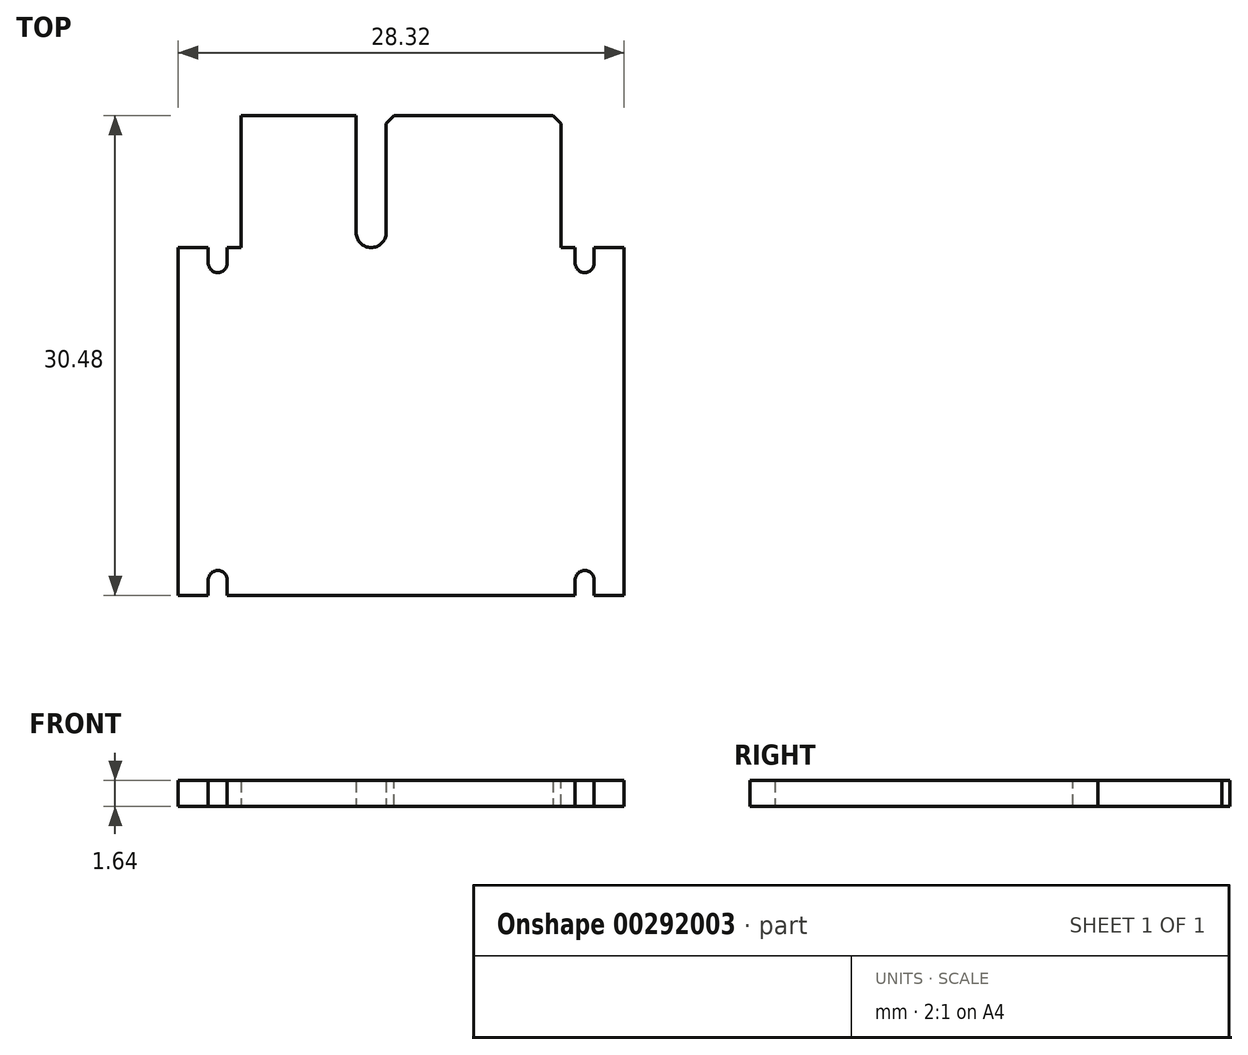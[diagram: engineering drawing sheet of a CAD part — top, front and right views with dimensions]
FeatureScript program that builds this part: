
annotation { "Feature Type Name" : "Feature", "Feature Type Description" : "" }
export const myFeature = defineFeature(function(context is Context, id is Id, definition is map)
    precondition{}
    {
        {
            var Q0;
            Q0=qCreatedBy(makeId("Top.planeOp"),FACE);
            var sketch = newSketch(context, id + "F0", { "sketchPlane" : qUnion([Q0])});
            skLineSegment(sketch, "E0.bottom", {"start": v(14.16, -30.48) * mm, "end": v(-14.16, -30.48) * mm});
            skLineSegment(sketch, "E0.top", {"start": v(14.16, 0) * mm, "end": v(-14.16, 0) * mm});
            skLineSegment(sketch, "E0.left", {"start": v(14.16, -30.48) * mm, "end": v(14.16, 0) * mm});
            skLineSegment(sketch, "E0.right", {"start": v(-14.16, -30.48) * mm, "end": v(-14.16, 0) * mm});
            skPoint(sketch, "E0.middle", {"position": v(0, 0) * mm});
            skSolve(sketch);
        }
        {
            var Q0;
            Q0=qSketchRegion(id+"F0",true);
            extrude(context, id + "F1", {"entities" : qUnion([Q0]), "depth" : 1.64 * mm});
        }
        {
            var Q0;
            Q0=qCreatedBy(makeId("Top.planeOp"),FACE);
            var sketch = newSketch(context, id + "F2", { "sketchPlane" : qUnion([Q0])});
            skLineSegment(sketch, "E1.top", {"start": v(-14.16, 0) * mm, "end": v(-10.16, 0) * mm});
            skLineSegment(sketch, "E1.left", {"start": v(-14.16, -8.38) * mm, "end": v(-14.16, 0) * mm});
            skLineSegment(sketch, "E1.right", {"start": v(-10.16, -8.38) * mm, "end": v(-10.16, 0) * mm});
            skLineSegment(sketch, "E2.bottom", {"start": v(-2.86, -8.38) * mm, "end": v(-0.95, -8.38) * mm});
            skLineSegment(sketch, "E2.top", {"start": v(-2.86, 0) * mm, "end": v(-0.95, 0) * mm});
            skLineSegment(sketch, "E2.left", {"start": v(-2.86, -8.38) * mm, "end": v(-2.86, 0) * mm});
            skLineSegment(sketch, "E2.right", {"start": v(-0.95, -8.38) * mm, "end": v(-0.95, 0) * mm});
            skLineSegment(sketch, "E3.top", {"start": v(14.16, 0) * mm, "end": v(10.16, 0) * mm});
            skLineSegment(sketch, "E3.left", {"start": v(14.16, -8.38) * mm, "end": v(14.16, 0) * mm});
            skLineSegment(sketch, "E3.right", {"start": v(10.16, -8.38) * mm, "end": v(10.16, 0) * mm});
            skLineSegment(sketch, "E4", {"start": v(-14.16, -8.38) * mm, "end": v(-12.26, -8.38) * mm});
            skLineSegment(sketch, "E5", {"start": v(-12.26, -8.38) * mm, "end": v(-12.26, -9.97) * mm});
            skLineSegment(sketch, "E6", {"start": v(-12.26, -9.97) * mm, "end": v(-11.05, -9.97) * mm});
            skLineSegment(sketch, "E7", {"start": v(-11.05, -9.97) * mm, "end": v(-11.05, -8.38) * mm});
            skLineSegment(sketch, "E8", {"start": v(-11.05, -8.38) * mm, "end": v(-10.16, -8.38) * mm});
            skLineSegment(sketch, "E9", {"start": v(10.16, -8.38) * mm, "end": v(11.05, -8.38) * mm});
            skLineSegment(sketch, "E10", {"start": v(11.05, -8.38) * mm, "end": v(11.05, -9.97) * mm});
            skLineSegment(sketch, "E11", {"start": v(11.05, -9.97) * mm, "end": v(12.26, -9.97) * mm});
            skLineSegment(sketch, "E12", {"start": v(12.26, -9.97) * mm, "end": v(12.26, -8.38) * mm});
            skLineSegment(sketch, "E13", {"start": v(12.26, -8.38) * mm, "end": v(14.16, -8.38) * mm});
            skLineSegment(sketch, "E14.bottom", {"start": v(-12.26, -30.48) * mm, "end": v(-11.05, -30.48) * mm});
            skLineSegment(sketch, "E14.top", {"start": v(-12.26, -28.9) * mm, "end": v(-11.05, -28.9) * mm});
            skLineSegment(sketch, "E14.left", {"start": v(-12.26, -30.48) * mm, "end": v(-12.26, -28.9) * mm});
            skLineSegment(sketch, "E14.right", {"start": v(-11.05, -30.48) * mm, "end": v(-11.05, -28.9) * mm});
            skLineSegment(sketch, "E15.bottom", {"start": v(11.05, -30.48) * mm, "end": v(12.26, -30.48) * mm});
            skLineSegment(sketch, "E15.top", {"start": v(11.05, -28.9) * mm, "end": v(12.26, -28.9) * mm});
            skLineSegment(sketch, "E15.left", {"start": v(11.05, -30.48) * mm, "end": v(11.05, -28.9) * mm});
            skLineSegment(sketch, "E15.right", {"start": v(12.26, -30.48) * mm, "end": v(12.26, -28.9) * mm});
            skLineSegment(sketch, "E16", {"start": v(-20.57, -19.43) * mm, "end": v(25.43, -19.43) * mm, "construction": true});
            skSolve(sketch);
        }
        {
            var Q0;
            Q0=qSketchRegion(id+"F2",true);
            extrude(context, id + "F3", {"entities" : qUnion([Q0]), "operationType" : NewBodyOperationType.REMOVE, "depth" : 25 * mm});
        }
        {
            var Q0;
            Q0=makeQuery(id+"F3.boolean.opBoolean","COPY",EDGE,{"derivedFrom":makeQuery(id+"F3.opExtrude","SWEPT_EDGE",EDGE,{"disambiguationData":[OSD([sQuery(id+"F2.wireOp",EDGE,"E2.bottom"),sQuery(id+"F2.wireOp",EDGE,"E2.left")])]})});
            var Q1;
            Q1=makeQuery(id+"F3.boolean.opBoolean","COPY",EDGE,{"derivedFrom":makeQuery(id+"F3.opExtrude","SWEPT_EDGE",EDGE,{"disambiguationData":[OSD([sQuery(id+"F2.wireOp",EDGE,"E2.bottom"),sQuery(id+"F2.wireOp",EDGE,"E2.right")])]})});
            fillet(context, id + "F4", {"entities" : qUnion([Q0, Q1]), "radius" : (1.9 / 2) * mm, "tangentPropagation" : true, "allowEdgeOverflow" : false});
        }
        {
            var Q0;
            Q0=makeQuery(id+"F3.boolean.opBoolean","COPY",EDGE,{"derivedFrom":makeQuery(id+"F3.opExtrude","SWEPT_EDGE",EDGE,{"disambiguationData":[OSD([sQuery(id+"F2.wireOp",EDGE,"E3.top"),sQuery(id+"F2.wireOp",EDGE,"E3.right")])]})});
            var Q1;
            Q1=makeQuery(id+"F3.boolean.opBoolean","COPY",EDGE,{"derivedFrom":makeQuery(id+"F3.opExtrude","SWEPT_EDGE",EDGE,{"disambiguationData":[OSD([sQuery(id+"F2.wireOp",EDGE,"E2.top"),sQuery(id+"F2.wireOp",EDGE,"E2.right")])]})});
            var Q2;
            Q2=makeQuery(id+"F3.boolean.opBoolean","COPY",EDGE,{"derivedFrom":makeQuery(id+"F3.opExtrude","SWEPT_EDGE",EDGE,{"disambiguationData":[OSD([sQuery(id+"F2.wireOp",EDGE,"E2.top"),sQuery(id+"F2.wireOp",EDGE,"E2.left")])]})});
            var Q3;
            Q3=makeQuery(id+"F3.boolean.opBoolean","COPY",EDGE,{"derivedFrom":makeQuery(id+"F3.opExtrude","SWEPT_EDGE",EDGE,{"disambiguationData":[OSD([sQuery(id+"F2.wireOp",EDGE,"E1.top"),sQuery(id+"F2.wireOp",EDGE,"E1.right")])]})});
            chamfer(context, id + "F5", {"entities" : qUnion([Q0, Q1, Q2, Q3]), "width" : 0.5 * mm, "tangentPropagation" : true});
        }
        {
            var Q0;
            Q0=makeQuery(id+"F3.boolean.opBoolean","COPY",EDGE,{"derivedFrom":makeQuery(id+"F3.opExtrude","SWEPT_EDGE",EDGE,{"disambiguationData":[OSD([sQuery(id+"F2.wireOp",EDGE,"E15.top"),sQuery(id+"F2.wireOp",EDGE,"E15.right")])]})});
            var Q1;
            Q1=makeQuery(id+"F3.boolean.opBoolean","COPY",EDGE,{"derivedFrom":makeQuery(id+"F3.opExtrude","SWEPT_EDGE",EDGE,{"disambiguationData":[OSD([sQuery(id+"F2.wireOp",EDGE,"E14.top"),sQuery(id+"F2.wireOp",EDGE,"E14.left")])]})});
            var Q2;
            Q2=makeQuery(id+"F3.boolean.opBoolean","COPY",EDGE,{"derivedFrom":makeQuery(id+"F3.opExtrude","SWEPT_EDGE",EDGE,{"disambiguationData":[OSD([sQuery(id+"F2.wireOp",EDGE,"E14.top"),sQuery(id+"F2.wireOp",EDGE,"E14.right")])]})});
            var Q3;
            Q3=makeQuery(id+"F3.boolean.opBoolean","COPY",EDGE,{"derivedFrom":makeQuery(id+"F3.opExtrude","SWEPT_EDGE",EDGE,{"disambiguationData":[OSD([sQuery(id+"F2.wireOp",EDGE,"E15.top"),sQuery(id+"F2.wireOp",EDGE,"E15.left")])]})});
            var Q4;
            Q4=makeQuery(id+"F3.boolean.opBoolean","COPY",EDGE,{"derivedFrom":makeQuery(id+"F3.opExtrude","SWEPT_EDGE",EDGE,{"disambiguationData":[OSD([sQuery(id+"F2.wireOp",EDGE,"E10"),sQuery(id+"F2.wireOp",EDGE,"E11")])]})});
            var Q5;
            Q5=makeQuery(id+"F3.boolean.opBoolean","COPY",EDGE,{"derivedFrom":makeQuery(id+"F3.opExtrude","SWEPT_EDGE",EDGE,{"disambiguationData":[OSD([sQuery(id+"F2.wireOp",EDGE,"E11"),sQuery(id+"F2.wireOp",EDGE,"E12")])]})});
            var Q6;
            Q6=makeQuery(id+"F3.boolean.opBoolean","COPY",EDGE,{"derivedFrom":makeQuery(id+"F3.opExtrude","SWEPT_EDGE",EDGE,{"disambiguationData":[OSD([sQuery(id+"F2.wireOp",EDGE,"E5"),sQuery(id+"F2.wireOp",EDGE,"E6")])]})});
            var Q7;
            Q7=makeQuery(id+"F3.boolean.opBoolean","COPY",EDGE,{"derivedFrom":makeQuery(id+"F3.opExtrude","SWEPT_EDGE",EDGE,{"disambiguationData":[OSD([sQuery(id+"F2.wireOp",EDGE,"E6"),sQuery(id+"F2.wireOp",EDGE,"E7")])]})});
            fillet(context, id + "F6", {"entities" : qUnion([Q0, Q1, Q2, Q3, Q4, Q5, Q6, Q7]), "radius" : (1.2 / 2) * mm, "tangentPropagation" : true, "allowEdgeOverflow" : false});
        }
    });
